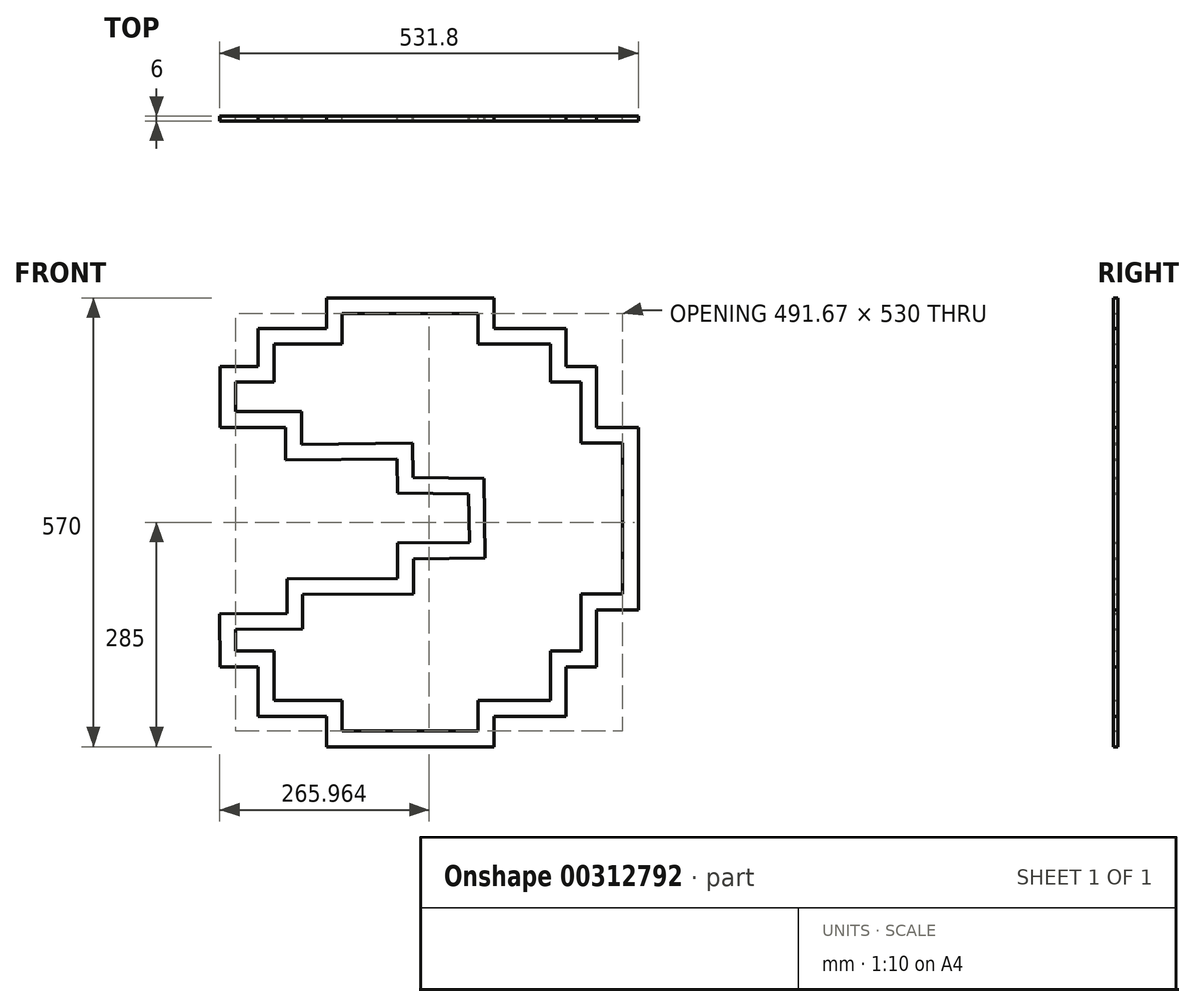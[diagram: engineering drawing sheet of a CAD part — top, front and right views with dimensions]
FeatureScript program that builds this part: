
annotation { "Feature Type Name" : "Feature", "Feature Type Description" : "" }
export const myFeature = defineFeature(function(context is Context, id is Id, definition is map)
    precondition{}
    {
        {
            var Q0;
            Q0=qCreatedBy(makeId("Front.planeOp"),FACE);
            var sketch = newSketch(context, id + "F0", { "sketchPlane" : qUnion([Q0])});
            skLineSegment(sketch, "E0", {"start": v(265.9, 120.76) * mm, "end": v(212.76, 120.76) * mm});
            skLineSegment(sketch, "E1", {"start": v(212.76, 120.76) * mm, "end": v(212.76, 198.05) * mm});
            skLineSegment(sketch, "E2", {"start": v(212.76, 198.05) * mm, "end": v(174.11, 198.05) * mm});
            skLineSegment(sketch, "E3", {"start": v(174.11, 198.05) * mm, "end": v(174.11, 246.35) * mm});
            skLineSegment(sketch, "E4", {"start": v(174.11, 246.35) * mm, "end": v(82.34, 246.35) * mm});
            skLineSegment(sketch, "E5", {"start": v(82.34, 246.35) * mm, "end": v(82.34, 285) * mm});
            skLineSegment(sketch, "E6", {"start": v(82.34, 285) * mm, "end": v(-130.2, 285) * mm});
            skLineSegment(sketch, "E7", {"start": v(-130.2, 285) * mm, "end": v(-130.2, 246.35) * mm});
            skLineSegment(sketch, "E8", {"start": v(-130.2, 246.35) * mm, "end": v(-217.15, 246.35) * mm});
            skLineSegment(sketch, "E9", {"start": v(-217.15, 246.35) * mm, "end": v(-217.15, 198.05) * mm});
            skLineSegment(sketch, "E10", {"start": v(-217.15, 198.05) * mm, "end": v(-265.46, 198.05) * mm});
            skLineSegment(sketch, "E11", {"start": v(-265.46, 198.05) * mm, "end": v(-265.46, 120.76) * mm});
            skLineSegment(sketch, "E12", {"start": v(-265.46, 120.76) * mm, "end": v(-182.22, 120.66) * mm});
            skLineSegment(sketch, "E13", {"start": v(-182.22, 120.66) * mm, "end": v(-182.3, 79) * mm});
            skLineSegment(sketch, "E14", {"start": v(-182.3, 79) * mm, "end": v(-40.62, 80.76) * mm});
            skLineSegment(sketch, "E15", {"start": v(-40.62, 80.76) * mm, "end": v(-39.72, 37.15) * mm});
            skLineSegment(sketch, "E16", {"start": v(-39.72, 37.15) * mm, "end": v(50.2, 36.25) * mm});
            skLineSegment(sketch, "E17", {"start": v(50.2, 36.25) * mm, "end": v(51.12, -25.52) * mm});
            skLineSegment(sketch, "E18", {"start": v(51.12, -25.52) * mm, "end": v(-39.72, -26.43) * mm});
            skLineSegment(sketch, "E19", {"start": v(-39.72, -26.43) * mm, "end": v(-39.72, -70.94) * mm});
            skLineSegment(sketch, "E20", {"start": v(-39.72, -70.94) * mm, "end": v(-180.51, -71.85) * mm});
            skLineSegment(sketch, "E21", {"start": v(-180.51, -71.85) * mm, "end": v(-180.51, -115.45) * mm});
            skLineSegment(sketch, "E22", {"start": v(-180.51, -115.45) * mm, "end": v(-265.9, -116.36) * mm});
            skLineSegment(sketch, "E23", {"start": v(-265.9, -116.36) * mm, "end": v(-265.46, -183.56) * mm});
            skLineSegment(sketch, "E24", {"start": v(-265.46, -183.56) * mm, "end": v(-217.15, -183.56) * mm});
            skLineSegment(sketch, "E25", {"start": v(-217.15, -183.56) * mm, "end": v(-217.15, -246.36) * mm});
            skLineSegment(sketch, "E26", {"start": v(-217.15, -246.36) * mm, "end": v(-130.2, -246.36) * mm});
            skLineSegment(sketch, "E27", {"start": v(-130.2, -246.36) * mm, "end": v(-130.2, -285) * mm});
            skLineSegment(sketch, "E28", {"start": v(-130.2, -285) * mm, "end": v(82.34, -285) * mm});
            skLineSegment(sketch, "E29", {"start": v(82.34, -285) * mm, "end": v(82.34, -246.36) * mm});
            skLineSegment(sketch, "E30", {"start": v(82.34, -246.36) * mm, "end": v(174.11, -246.36) * mm});
            skLineSegment(sketch, "E31", {"start": v(174.11, -246.36) * mm, "end": v(174.11, -183.56) * mm});
            skLineSegment(sketch, "E32", {"start": v(174.11, -183.56) * mm, "end": v(212.76, -183.56) * mm});
            skLineSegment(sketch, "E33", {"start": v(212.76, -183.56) * mm, "end": v(212.76, -111.1) * mm});
            skLineSegment(sketch, "E34", {"start": v(212.76, -111.1) * mm, "end": v(265.9, -111.1) * mm});
            skLineSegment(sketch, "E35", {"start": v(265.9, -111.1) * mm, "end": v(265.9, 120.76) * mm});
            skLineSegment(sketch, "E36.0", {"start": v(-160.51, -91.72) * mm, "end": v(-160.51, -135.23) * mm});
            skLineSegment(sketch, "E36.1", {"start": v(-19.72, -90.8) * mm, "end": v(-160.51, -91.72) * mm});
            skLineSegment(sketch, "E36.2", {"start": v(-19.72, -46.23) * mm, "end": v(-19.72, -90.8) * mm});
            skLineSegment(sketch, "E36.3", {"start": v(71.42, -45.32) * mm, "end": v(-19.72, -46.23) * mm});
            skLineSegment(sketch, "E36.4", {"start": v(69.92, 56.05) * mm, "end": v(71.42, -45.32) * mm});
            skLineSegment(sketch, "E36.5", {"start": v(-20.12, 56.96) * mm, "end": v(69.92, 56.05) * mm});
            skLineSegment(sketch, "E36.6", {"start": v(-21.04, 101) * mm, "end": v(-20.12, 56.96) * mm});
            skLineSegment(sketch, "E36.7", {"start": v(-162.25, 99.25) * mm, "end": v(-21.04, 101) * mm});
            skLineSegment(sketch, "E36.8", {"start": v(-162.18, 140.63) * mm, "end": v(-162.25, 99.25) * mm});
            skLineSegment(sketch, "E36.9", {"start": v(-245.46, 140.74) * mm, "end": v(-162.18, 140.63) * mm});
            skLineSegment(sketch, "E36.10", {"start": v(-245.46, 178.05) * mm, "end": v(-245.46, 140.74) * mm});
            skLineSegment(sketch, "E36.11", {"start": v(-160.51, -135.23) * mm, "end": v(-245.77, -136.15) * mm});
            skLineSegment(sketch, "E36.12", {"start": v(-197.15, 178.05) * mm, "end": v(-245.46, 178.05) * mm});
            skLineSegment(sketch, "E36.13", {"start": v(-197.15, 226.35) * mm, "end": v(-197.15, 178.05) * mm});
            skLineSegment(sketch, "E36.14", {"start": v(154.11, -163.56) * mm, "end": v(192.76, -163.56) * mm});
            skLineSegment(sketch, "E36.15", {"start": v(154.11, -226.36) * mm, "end": v(154.11, -163.56) * mm});
            skLineSegment(sketch, "E36.16", {"start": v(62.34, -226.36) * mm, "end": v(154.11, -226.36) * mm});
            skLineSegment(sketch, "E36.17", {"start": v(62.34, -265) * mm, "end": v(62.34, -226.36) * mm});
            skLineSegment(sketch, "E36.18", {"start": v(-110.2, -265) * mm, "end": v(62.34, -265) * mm});
            skLineSegment(sketch, "E36.19", {"start": v(-110.2, -226.36) * mm, "end": v(-110.2, -265) * mm});
            skLineSegment(sketch, "E36.20", {"start": v(-245.77, -136.15) * mm, "end": v(-245.6, -163.56) * mm});
            skLineSegment(sketch, "E36.21", {"start": v(-245.6, -163.56) * mm, "end": v(-197.15, -163.56) * mm});
            skLineSegment(sketch, "E36.22", {"start": v(-197.15, -163.56) * mm, "end": v(-197.15, -226.36) * mm});
            skLineSegment(sketch, "E36.23", {"start": v(-197.15, -226.36) * mm, "end": v(-110.2, -226.36) * mm});
            skLineSegment(sketch, "E36.24", {"start": v(192.76, -163.56) * mm, "end": v(192.76, -91.1) * mm});
            skLineSegment(sketch, "E36.25", {"start": v(192.76, -91.1) * mm, "end": v(245.9, -91.1) * mm});
            skLineSegment(sketch, "E36.26", {"start": v(245.9, -91.1) * mm, "end": v(245.9, 100.76) * mm});
            skLineSegment(sketch, "E36.27", {"start": v(245.9, 100.76) * mm, "end": v(192.76, 100.76) * mm});
            skLineSegment(sketch, "E36.28", {"start": v(192.76, 100.76) * mm, "end": v(192.76, 178.05) * mm});
            skLineSegment(sketch, "E36.29", {"start": v(192.76, 178.05) * mm, "end": v(154.11, 178.05) * mm});
            skLineSegment(sketch, "E36.30", {"start": v(154.11, 178.05) * mm, "end": v(154.11, 226.35) * mm});
            skLineSegment(sketch, "E36.31", {"start": v(154.11, 226.35) * mm, "end": v(62.34, 226.35) * mm});
            skLineSegment(sketch, "E36.32", {"start": v(62.34, 226.35) * mm, "end": v(62.34, 265) * mm});
            skLineSegment(sketch, "E36.33", {"start": v(62.34, 265) * mm, "end": v(-110.2, 265) * mm});
            skLineSegment(sketch, "E36.34", {"start": v(-110.2, 265) * mm, "end": v(-110.2, 226.35) * mm});
            skLineSegment(sketch, "E36.35", {"start": v(-110.2, 226.35) * mm, "end": v(-197.15, 226.35) * mm});
            skSolve(sketch);
        }
        {
            var Q0;
            Q0=makeQuery(id+"F0.imprint","IMPRINT",FACE,{"disambiguationData":[TD([[makeQuery(id+"F0.imprint","IMPRINT",EDGE,{"derivedFrom":sQuery(id+"F0.wireOp",EDGE,"E0")}),1.0]])]});
            extrude(context, id + "F1", {"entities" : qUnion([Q0]), "depth" : 6 * mm});
        }
    });
